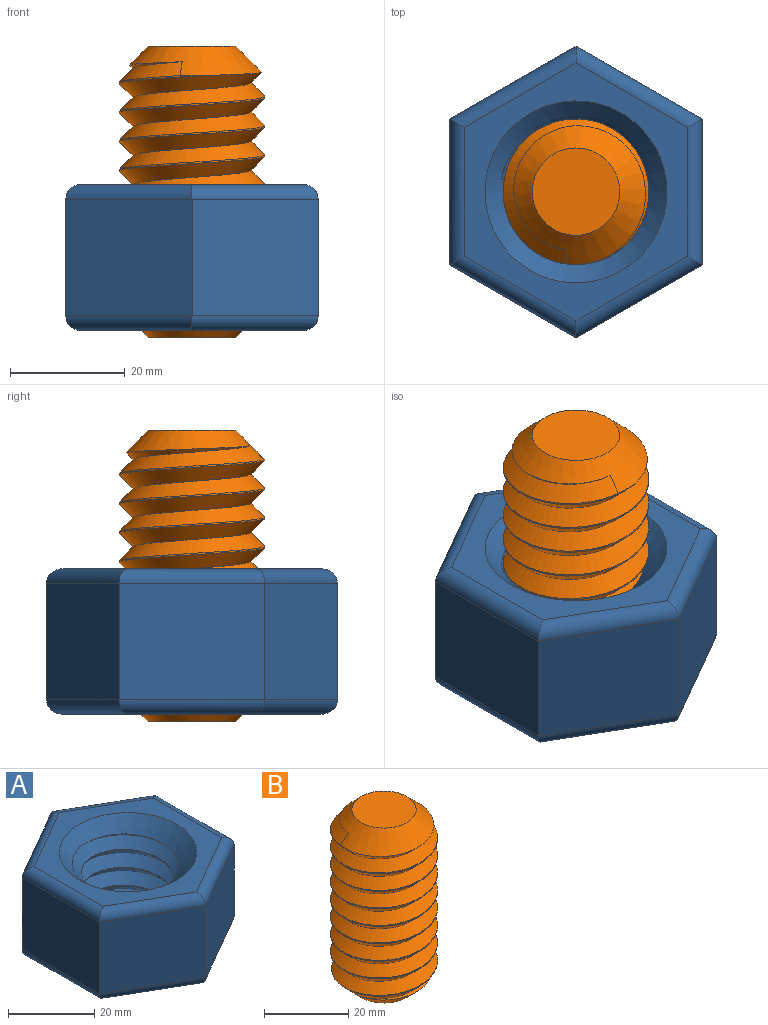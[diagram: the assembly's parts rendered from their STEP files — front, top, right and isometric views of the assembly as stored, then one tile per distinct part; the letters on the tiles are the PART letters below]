
ASSEMBLY  parts=2 mates=1
PART A: 25 faces, bbox 44x50.8x25.4 mm
  f0: plane 44.93x38.91mm, normal (0,0,-1), area 519.7mm2, adj f12,f13,f14,f15,f16,f17,f18
  f1: plane 22x20.32mm, normal (0.5,0.87,0), area 516.1mm2, adj f2,f6,f16,f22
  f2: plane 22x20.32mm, normal (-0.5,0.87,0), area 516.1mm2, adj f1,f3,f14,f20
  f3: plane 25.4x20.32mm, normal (-1,0,0), area 516.1mm2, adj f2,f4,f13,f19
  f4: plane 22x20.32mm, normal (-0.5,-0.87,0), area 516.1mm2, adj f3,f5,f15,f21
  f5: plane 22x20.32mm, normal (0.5,-0.87,0), area 516.1mm2, adj f4,f6,f17,f23
  f6: plane 25.4x20.32mm, normal (1,0,0), area 516.1mm2, adj f1,f5,f18,f24
  f7: cylinder r=10.79mm len=21.59mm, axis (0,0,-1), area 51.9mm2, adj f9,f10,f11,f12
  f8: plane 44.93x38.91mm, normal (0,0,1), area 519.7mm2, adj f11,f19,f20,f21,f22,f23,f24
  f9: bspline ~30.5x26.42mm, area 899.1mm2, adj f7,f10,f11,f12
  f10: bspline ~30.5x26.42mm, area 899.6mm2, adj f7,f9,f11,f12
  f11: cone r=10.79mm half-angle=45deg, axis (0,0,1), area 484.2mm2, adj f7,f8,f9,f10
  f12: cone r=15.88mm half-angle=45deg, axis (0,0,-1), area 484.2mm2, adj f0,f7,f9,f10
  f13: cylinder r=2.54mm len=25.4mm, axis (0,-1,0), area 95.5mm2, adj f0,f3,f14,f15
  f14: cylinder r=2.54mm len=23.27mm, axis (-0.87,-0.5,0), area 95.5mm2, adj f0,f2,f13,f16
  f15: cylinder r=2.54mm len=23.27mm, axis (0.87,-0.5,0), area 95.5mm2, adj f0,f4,f13,f17
  f16: cylinder r=2.54mm len=23.27mm, axis (-0.87,0.5,0), area 95.5mm2, adj f0,f1,f14,f18
  f17: cylinder r=2.54mm len=23.27mm, axis (0.87,0.5,0), area 95.5mm2, adj f0,f5,f15,f18
  f18: cylinder r=2.54mm len=25.4mm, axis (0,1,0), area 95.5mm2, adj f0,f6,f16,f17
  f19: cylinder r=2.54mm len=25.4mm, axis (0,1,0), area 95.5mm2, adj f3,f8,f20,f21
  f20: cylinder r=2.54mm len=23.27mm, axis (0.87,0.5,0), area 95.5mm2, adj f2,f8,f19,f22
  f21: cylinder r=2.54mm len=23.27mm, axis (-0.87,0.5,0), area 95.5mm2, adj f4,f8,f19,f23
  f22: cylinder r=2.54mm len=23.27mm, axis (0.87,-0.5,0), area 95.5mm2, adj f1,f8,f20,f24
  f23: cylinder r=2.54mm len=23.27mm, axis (-0.87,-0.5,0), area 95.5mm2, adj f5,f8,f21,f24
  f24: cylinder r=2.54mm len=25.4mm, axis (0,-1,0), area 95.5mm2, adj f6,f8,f22,f23
PART B: 7 faces, bbox 25.4x29.3x50.8 mm
  f0: cylinder r=12.7mm len=40.64mm, axis (0,0,-1), area -53mm2, adj f3,f4,f5,f6
  f1: plane 15.24x15.24mm, normal (0,0,1), area 182.4mm2, adj f5
  f2: plane 15.24x15.24mm, normal (0,0,-1), area 182.4mm2, adj f6
  f3: bspline ~48.13x29.33mm, area 2088.9mm2, adj f0,f4,f5,f6
  f4: bspline ~48.13x29.33mm, area 2097.2mm2, adj f0,f3,f5,f6
  f5: cone r=7.62mm half-angle=45deg, axis (0,0,-1), area 337.8mm2, adj f0,f1,f3,f4
  f6: cone r=12.7mm half-angle=45deg, axis (0,0,1), area 337.8mm2, adj f0,f2,f3,f4
PLACE A t=(0,0,-11.43)mm
PLACE B rot(axis=(0,0,1),90deg) t=(0,0,0)mm
MATE cylindrical A.f7 <-> B.f0  axis (0,0,-1) through (0,0,-24.13)mm
